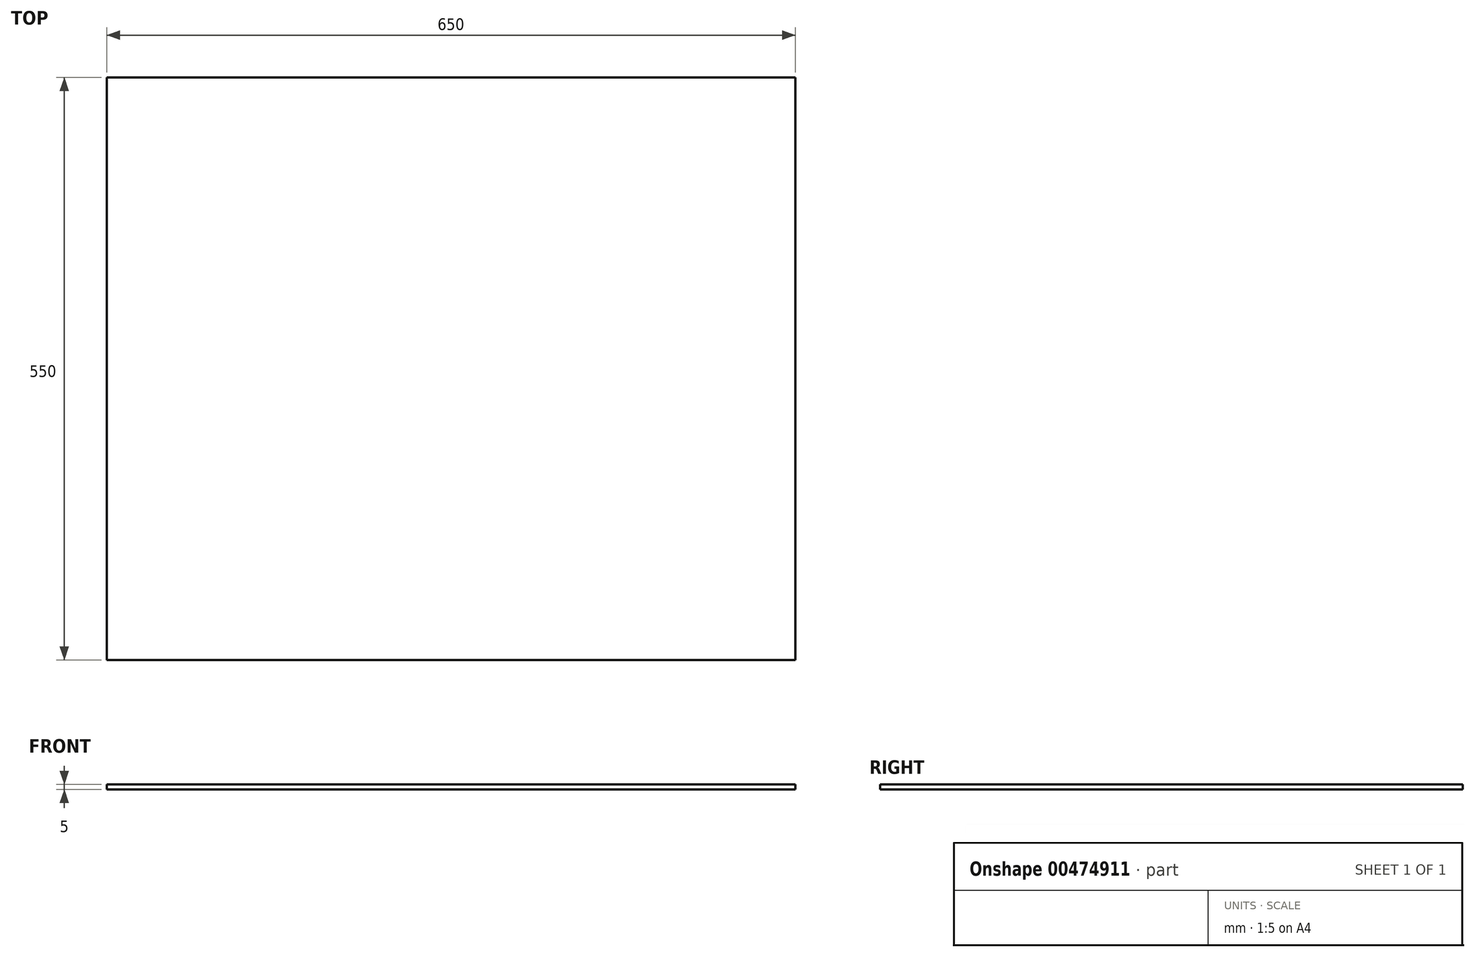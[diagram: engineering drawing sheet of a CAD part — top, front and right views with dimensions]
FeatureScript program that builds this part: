
annotation { "Feature Type Name" : "Feature", "Feature Type Description" : "" }
export const myFeature = defineFeature(function(context is Context, id is Id, definition is map)
    precondition{}
    {
        {
            var Q0;
            Q0=qCreatedBy(makeId("Top.planeOp"),FACE);
            var sketch = newSketch(context, id + "F0", { "sketchPlane" : qUnion([Q0])});
            skLineSegment(sketch, "E0.bottom", {"start": v(-336.36, 226.6) * mm, "end": v(313.64, 226.6) * mm});
            skLineSegment(sketch, "E0.top", {"start": v(-336.36, -323.4) * mm, "end": v(313.64, -323.4) * mm});
            skLineSegment(sketch, "E0.left", {"start": v(-336.36, 226.6) * mm, "end": v(-336.36, -323.4) * mm});
            skLineSegment(sketch, "E0.right", {"start": v(313.64, 226.6) * mm, "end": v(313.64, -323.4) * mm});
            skSolve(sketch);
        }
        {
            var Q0;
            Q0=makeQuery(id+"F0.imprint","IMPRINT",FACE,{"disambiguationData":[TD([[makeQuery(id+"F0.imprint","IMPRINT",EDGE,{"derivedFrom":sQuery(id+"F0.wireOp",EDGE,"E0.bottom")}),-1.0]])]});
            extrude(context, id + "F1", {"entities" : qUnion([Q0]), "depth" : 5 * mm, "offsetDistance" : 25 * mm});
        }
    });
